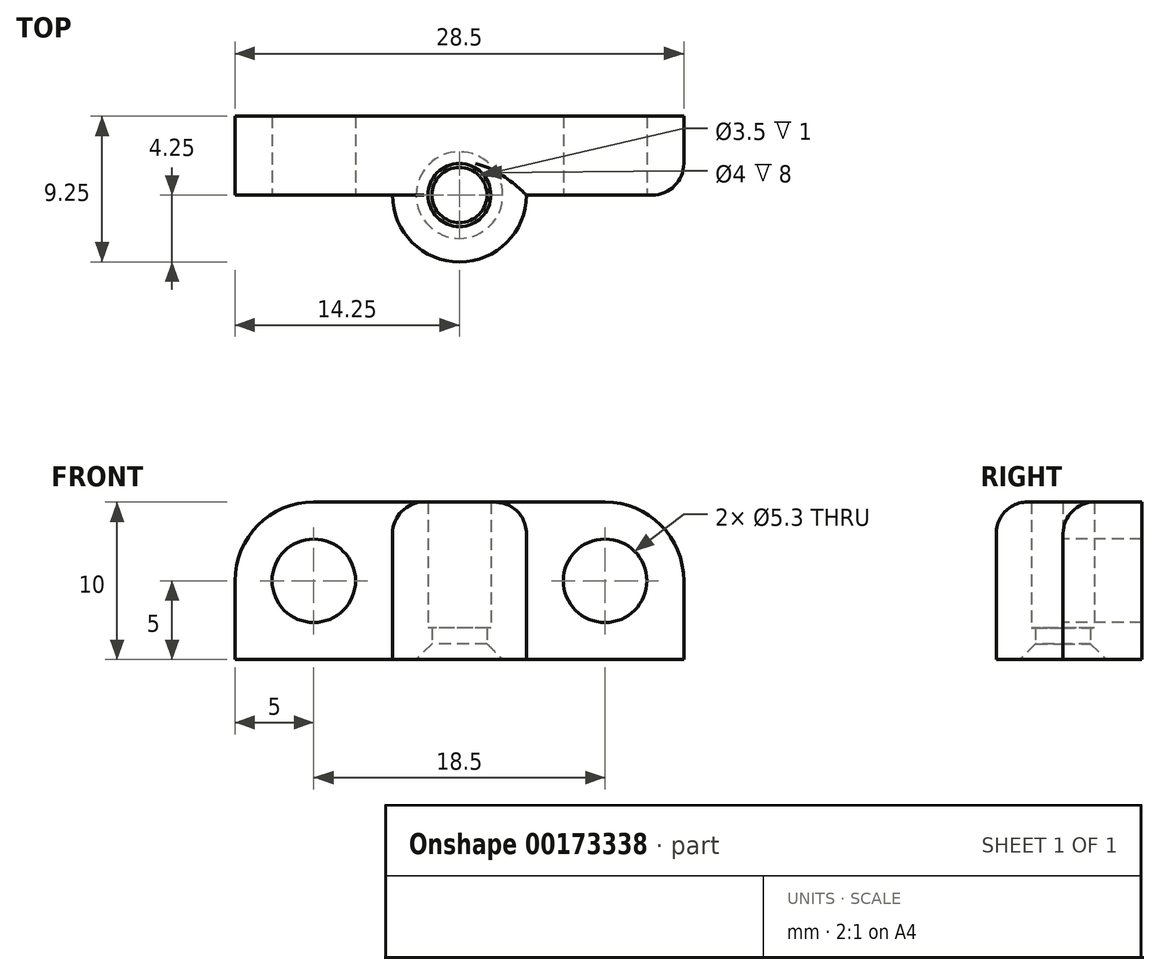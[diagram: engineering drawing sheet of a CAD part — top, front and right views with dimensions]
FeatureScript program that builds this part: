
annotation { "Feature Type Name" : "Feature", "Feature Type Description" : "" }
export const myFeature = defineFeature(function(context is Context, id is Id, definition is map)
    precondition{}
    {
        {
            var Q0;
            Q0=qCreatedBy(makeId("Top.planeOp"),FACE);
            var sketch = newSketch(context, id + "F0", { "sketchPlane" : qUnion([Q0])});
            skCircle(sketch, "E0", {"center": v(0, 0) * mm, "radius": 4.25 * mm});
            skCircle(sketch, "E1", {"center": v(0, 0) * mm, "radius": 1.75 * mm});
            skSolve(sketch);
        }
        {
            var Q0;
            Q0=makeQuery(id+"F0.imprint","IMPRINT",FACE,{"disambiguationData":[TD([[makeQuery(id+"F0.imprint","IMPRINT",EDGE,{"derivedFrom":sQuery(id+"F0.wireOp",EDGE,"E0")}),1.0]])]});
            extrude(context, id + "F1", {"entities" : qUnion([Q0]), "depth" : 2 * mm});
        }
        {
            var Q0;
            Q0=makeQuery(id+"F1.opExtrude","CAP_FACE",FACE,{"disambiguationData":[OSD([sQuery(id+"F0.wireOp",EDGE,"E0"),sQuery(id+"F0.wireOp",EDGE,"E1")])],"isStart":false});
            var sketch = newSketch(context, id + "F2", { "sketchPlane" : qUnion([Q0])});
            skCircle(sketch, "E2", {"center": v(0, 0) * mm, "radius": 4.25 * mm});
            skCircle(sketch, "E3", {"center": v(0, 0) * mm, "radius": 2 * mm});
            skSolve(sketch);
        }
        {
            var Q0;
            Q0=makeQuery(id+"F2.imprint","IMPRINT",FACE,{"disambiguationData":[TD([[makeQuery(id+"F2.imprint","IMPRINT",EDGE,{"derivedFrom":sQuery(id+"F2.wireOp",EDGE,"E2")}),1.0]])]});
            extrude(context, id + "F3", {"entities" : qUnion([Q0]), "operationType" : NewBodyOperationType.ADD, "depth" : 8 * mm});
        }
        {
            var Q0;
            Q0=makeQuery(id+"F3.opExtrude","CAP_FACE",FACE,{"disambiguationData":[OSD([sQuery(id+"F2.wireOp",EDGE,"E2"),sQuery(id+"F2.wireOp",EDGE,"E3")])],"isStart":false});
            var sketch = newSketch(context, id + "F4", { "sketchPlane" : qUnion([Q0])});
            skLineSegment(sketch, "E4.bottom", {"start": v(-14.25, 5) * mm, "end": v(14.25, 5) * mm});
            skLineSegment(sketch, "E4.top", {"start": v(-14.25, 0) * mm, "end": v(14.25, 0) * mm});
            skLineSegment(sketch, "E4.left", {"start": v(-14.25, 5) * mm, "end": v(-14.25, 0) * mm});
            skLineSegment(sketch, "E4.right", {"start": v(14.25, 5) * mm, "end": v(14.25, 0) * mm});
            skSolve(sketch);
        }
        {
            var Q0;
            Q0=makeQuery(id+"F4.imprint","IMPRINT",FACE,{"disambiguationData":[TD([[makeQuery(id+"F4.imprint","IMPRINT",EDGE,{"derivedFrom":sQuery(id+"F4.wireOp",EDGE,"E4.bottom")}),-1.0]])]});
            extrude(context, id + "F5", {"entities" : qUnion([Q0]), "operationType" : NewBodyOperationType.ADD, "oppositeDirection" : true, "depth" : 10 * mm});
        }
        {
            var Q0;
            {var subQ0=sQuery(id+"F4.wireOp",EDGE,"E4.top");Q0=makeQuery(id+"F5.opExtrude","SWEPT_FACE",FACE,{"disambiguationData":[OSD([subQ0]),TDD([makeQuery(id+"F4.imprint","IMPRINT",EDGE,{"disambiguationData":[TD([[makeQuery(id+"F4.imprint","INTERSECT",VERTEX,{"derivedFrom":[subQ0,sQuery(id+"F4.wireOp",EDGE,"E4.left")]}),-1.0]])],"derivedFrom":subQ0})])]});}
            var sketch = newSketch(context, id + "F6", { "sketchPlane" : qUnion([Q0])});
            skCircle(sketch, "E5", {"center": v(-9.25, 5) * mm, "radius": 2.65 * mm});
            skPoint(sketch, "E5.centerSnap0", {"position": v(-4.25, 5) * mm});
            skCircle(sketch, "E6", {"center": v(9.25, 5) * mm, "radius": 2.65 * mm});
            skSolve(sketch);
        }
        {
            var Q0;
            Q0=makeQuery(id+"F6.imprint","IMPRINT",FACE,{"disambiguationData":[TD([[makeQuery(id+"F6.imprint","IMPRINT",EDGE,{"derivedFrom":sQuery(id+"F6.wireOp",EDGE,"E5")}),1.0]])]});
            var Q1;
            Q1=makeQuery(id+"F6.imprint","IMPRINT",FACE,{"disambiguationData":[TD([[makeQuery(id+"F6.imprint","IMPRINT",EDGE,{"derivedFrom":sQuery(id+"F6.wireOp",EDGE,"E6")}),1.0]])]});
            extrude(context, id + "F7", {"entities" : qUnion([Q0, Q1]), "operationType" : NewBodyOperationType.REMOVE, "oppositeDirection" : true, "depth" : 25 * mm});
        }
        {
            var Q0;
            {var subQ0=sQuery(id+"F4.wireOp",EDGE,"E4.top");Q0=makeQuery(id+"F5.opExtrude","SWEPT_FACE",FACE,{"disambiguationData":[OSD([subQ0]),TDD([makeQuery(id+"F4.imprint","IMPRINT",EDGE,{"disambiguationData":[TD([[makeQuery(id+"F4.imprint","INTERSECT",VERTEX,{"derivedFrom":[subQ0,sQuery(id+"F4.wireOp",EDGE,"E4.left")]}),-1.0]])],"derivedFrom":subQ0})])]});}
            var sketch = newSketch(context, id + "F8", { "sketchPlane" : qUnion([Q0])});
            skCircle(sketch, "E7", {"center": v(-9.25, 5) * mm, "radius": 5 * mm});
            skCircle(sketch, "E8", {"center": v(9.25, 5) * mm, "radius": 5 * mm});
            skLineSegment(sketch, "E9.bottom", {"start": v(14.25, 10) * mm, "end": v(4.25, 10) * mm});
            skLineSegment(sketch, "E9.top", {"start": v(14.25, 0) * mm, "end": v(4.25, 0) * mm});
            skLineSegment(sketch, "E9.left", {"start": v(14.25, 10) * mm, "end": v(14.25, 0) * mm});
            skLineSegment(sketch, "E9.right", {"start": v(4.25, 10) * mm, "end": v(4.25, 0) * mm});
            skSolve(sketch);
        }
        {
            var Q0;
            {var subQ0=sQuery(id+"F8.wireOp",EDGE,"E9.bottom");var subQ1=sQuery(id+"F8.wireOp",EDGE,"E8");var subQ2=makeQuery(id+"F8.imprint","INTERSECT",VERTEX,{"derivedFrom":[subQ1,subQ0]});Q0=makeQuery(id+"F8.imprint","IMPRINT",FACE,{"disambiguationData":[TD([[makeQuery(id+"F8.imprint","IMPRINT",EDGE,{"disambiguationData":[TD([[subQ2,1.0]])],"derivedFrom":subQ1}),-1.0]])]});}
            var Q1;
            {var subQ0=sQuery(id+"F8.wireOp",EDGE,"E7");var subQ1=sQuery(id+"F4.wireOp",EDGE,"E4.left");var subQ2=sQuery(id+"F4.wireOp",EDGE,"E4.top");var subQ5=makeQuery(id+"F5.opExtrude","SWEPT_EDGE",EDGE,{"disambiguationData":[OSD([subQ2,subQ1])]});var subQ6=makeQuery(id+"F8.imprint","INTERSECT",VERTEX,{"derivedFrom":[subQ5,subQ0]});Q1=makeQuery(id+"F8.imprint","IMPRINT",FACE,{"disambiguationData":[TD([[makeQuery(id+"F8.imprint","IMPRINT",EDGE,{"disambiguationData":[TD([[subQ6,1.0]])],"derivedFrom":subQ0}),-1.0]])]});}
            extrude(context, id + "F9", {"entities" : qUnion([Q0, Q1]), "operationType" : NewBodyOperationType.REMOVE, "oppositeDirection" : true, "depth" : 25 * mm});
        }
        {
            var Q0;
            Q0=makeQuery(id+"F9.boolean.opBoolean","COPY",EDGE,{"derivedFrom":makeQuery(id+"F9.opExtrude","CAP_EDGE",EDGE,{"disambiguationData":[OSD([sQuery(id+"F8.wireOp",EDGE,"E7")])],"isStart":true})});
            var Q1;
            {var subQ0=sQuery(id+"F4.wireOp",EDGE,"E4.top");Q1=makeQuery(id+"F5.opExtrude","CAP_EDGE",EDGE,{"disambiguationData":[OSD([subQ0]),TDD([makeQuery(id+"F4.imprint","IMPRINT",EDGE,{"disambiguationData":[TD([[makeQuery(id+"F4.imprint","INTERSECT",VERTEX,{"derivedFrom":[subQ0,sQuery(id+"F4.wireOp",EDGE,"E4.right")]}),1.0]])],"derivedFrom":subQ0})])],"isStart":true});}
            var Q2;
            Q2=makeQuery(id+"F3.opExtrude","CAP_EDGE",EDGE,{"disambiguationData":[OSD([sQuery(id+"F2.wireOp",EDGE,"E2")])],"isStart":false});
            fillet(context, id + "F10", {"entities" : qUnion([Q0, Q1, Q2]), "radius" : 2 * mm, "tangentPropagation" : true, "allowEdgeOverflow" : false});
        }
        {
            var Q0;
            Q0=makeQuery(id+"F1.opExtrude","CAP_EDGE",EDGE,{"disambiguationData":[OSD([sQuery(id+"F0.wireOp",EDGE,"E1")])],"isStart":true});
            chamfer(context, id + "F11", {"entities" : qUnion([Q0]), "width" : 1 * mm, "tangentPropagation" : true});
        }
    });
